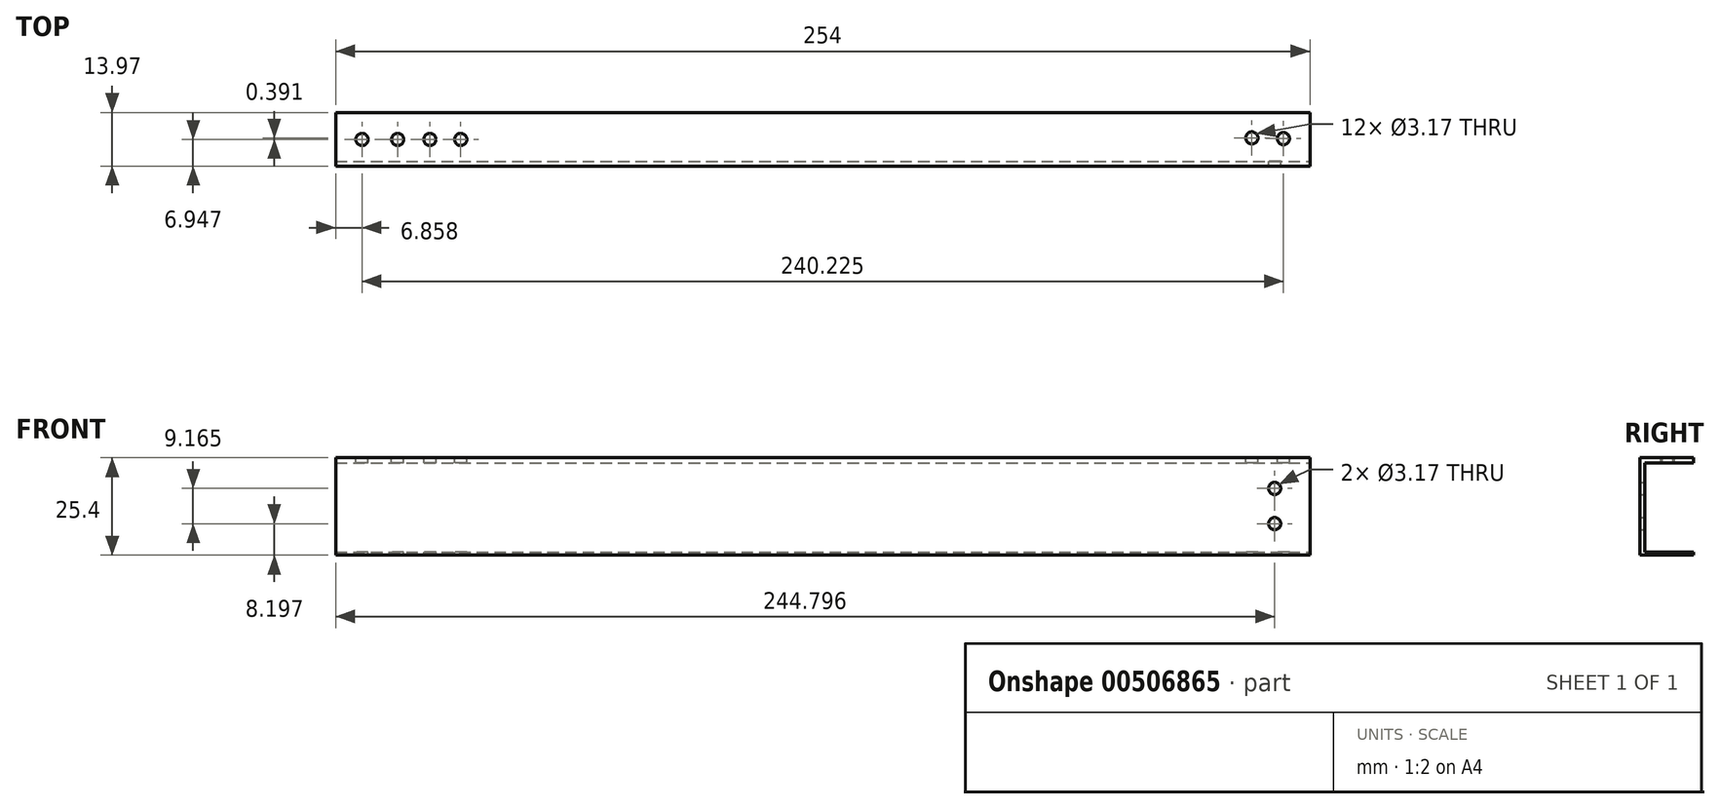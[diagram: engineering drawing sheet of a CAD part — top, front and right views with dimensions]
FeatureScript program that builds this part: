
annotation { "Feature Type Name" : "Feature", "Feature Type Description" : "" }
export const myFeature = defineFeature(function(context is Context, id is Id, definition is map)
    precondition{}
    {
        {
            var Q0;
            Q0=qCreatedBy(makeId("Front.planeOp"),FACE);
            var sketch = newSketch(context, id + "F0", { "sketchPlane" : qUnion([Q0])});
            skLineSegment(sketch, "E0.bottom", {"start": v(-123.25, 1.4) * mm, "end": v(130.75, 1.4) * mm});
            skLineSegment(sketch, "E0.top", {"start": v(-123.25, -24) * mm, "end": v(130.75, -24) * mm});
            skLineSegment(sketch, "E0.left", {"start": v(-123.25, 1.4) * mm, "end": v(-123.25, -24) * mm});
            skLineSegment(sketch, "E0.right", {"start": v(130.75, 1.4) * mm, "end": v(130.75, -24) * mm});
            skSolve(sketch);
        }
        {
            var Q0;
            Q0=makeQuery(id+"F0.imprint","IMPRINT",FACE,{"disambiguationData":[TD([[makeQuery(id+"F0.imprint","IMPRINT",EDGE,{"derivedFrom":sQuery(id+"F0.wireOp",EDGE,"E0.bottom")}),-1.0]])]});
            extrude(context, id + "F1", {"entities" : qUnion([Q0]), "depth" : 13.97 * mm, "offsetDistance" : 25.4 * mm});
        }
        {
            var Q0;
            Q0=qCreatedBy(makeId("Front.planeOp"),FACE);
            var sketch = newSketch(context, id + "F2", { "sketchPlane" : qUnion([Q0])});
            skLineSegment(sketch, "E1.bottom", {"start": v(-132.14, -23.19) * mm, "end": v(135.36, -23.19) * mm});
            skLineSegment(sketch, "E1.top", {"start": v(-132.14, 0) * mm, "end": v(135.36, 0) * mm});
            skLineSegment(sketch, "E1.left", {"start": v(-132.14, -23.19) * mm, "end": v(-132.14, 0) * mm});
            skLineSegment(sketch, "E1.right", {"start": v(135.36, -23.19) * mm, "end": v(135.36, 0) * mm});
            skSolve(sketch);
        }
        {
            var Q0;
            Q0=makeQuery(id+"F2.imprint","IMPRINT",FACE,{"disambiguationData":[TD([[makeQuery(id+"F2.imprint","IMPRINT",EDGE,{"derivedFrom":sQuery(id+"F2.wireOp",EDGE,"E1.bottom")}),1.0]])]});
            extrude(context, id + "F3", {"entities" : qUnion([Q0]), "operationType" : NewBodyOperationType.REMOVE, "depth" : 12.7 * mm, "offsetDistance" : 25.4 * mm});
        }
        {
            var Q0;
            Q0=makeQuery(id+"F1.opExtrude","SWEPT_FACE",FACE,{"disambiguationData":[OSD([sQuery(id+"F0.wireOp",EDGE,"E0.bottom")])]});
            var sketch = newSketch(context, id + "F4", { "sketchPlane" : qUnion([Q0])});
            skCircle(sketch, "E2", {"center": v(-116.4, -7.02) * mm, "radius": 2.87 * mm});
            skCircle(sketch, "E3", {"center": v(-107.1, -7.02) * mm, "radius": 2.68 * mm});
            skCircle(sketch, "E4", {"center": v(-98.69, -7.02) * mm, "radius": 2.66 * mm});
            skCircle(sketch, "E5", {"center": v(-90.64, -7.02) * mm, "radius": 2.91 * mm});
            skCircle(sketch, "E6", {"center": v(123.83, -6.82) * mm, "radius": 2.72 * mm});
            skCircle(sketch, "E7", {"center": v(115.61, -6.63) * mm, "radius": 3.06 * mm});
            skSolve(sketch);
        }
        {
            var Q0;
            Q0=sQuery(id+"F4.wireOp",VERTEX,"E6.center");
            var Q1;
            Q1=sQuery(id+"F4.wireOp",VERTEX,"E7.center");
            var Q2;
            Q2=sQuery(id+"F4.wireOp",VERTEX,"E2.center");
            var Q3;
            Q3=sQuery(id+"F4.wireOp",VERTEX,"E3.center");
            var Q4;
            Q4=sQuery(id+"F4.wireOp",VERTEX,"E4.center");
            var Q5;
            Q5=sQuery(id+"F4.wireOp",VERTEX,"E5.center");
            var Q6;
            Q6=makeQuery(id+"F1.opExtrude","SWEPT_BODY",BODY,{"disambiguationData":[OSD([sQuery(id+"F0.wireOp",EDGE,"E0.bottom"),sQuery(id+"F0.wireOp",EDGE,"E0.top"),sQuery(id+"F0.wireOp",EDGE,"E0.left"),sQuery(id+"F0.wireOp",EDGE,"E0.right")])]});
            hole(context, id + "F5", {"style" : HoleStyle.SIMPLE, "endStyle" : HoleEndStyle.THROUGH, "holeDiameter" : 3.17 * mm, "isTappedThrough" : true, "tappedDepth" : 12.7 * mm, "tapClearance" : 3, "locations" : qUnion([Q0, Q1, Q2, Q3, Q4, Q5]), "scope" : qUnion([Q6])});
        }
        {
            var Q0;
            Q0=qCreatedBy(makeId("Front.planeOp"),FACE);
            var sketch = newSketch(context, id + "F6", { "sketchPlane" : qUnion([Q0])});
            skCircle(sketch, "E8", {"center": v(121.55, -6.64) * mm, "radius": 2.16 * mm});
            skCircle(sketch, "E9", {"center": v(121.55, -15.8) * mm, "radius": 2.6 * mm});
            skSolve(sketch);
        }
        {
            var Q0;
            Q0=sQuery(id+"F6.wireOp",VERTEX,"E8.center");
            var Q1;
            Q1=sQuery(id+"F6.wireOp",VERTEX,"E9.center");
            var Q2;
            Q2=makeQuery(id+"F1.opExtrude","SWEPT_BODY",BODY,{"disambiguationData":[OSD([sQuery(id+"F0.wireOp",EDGE,"E0.bottom"),sQuery(id+"F0.wireOp",EDGE,"E0.top"),sQuery(id+"F0.wireOp",EDGE,"E0.left"),sQuery(id+"F0.wireOp",EDGE,"E0.right")])]});
            hole(context, id + "F7", {"style" : HoleStyle.SIMPLE, "endStyle" : HoleEndStyle.THROUGH, "oppositeDirection" : true, "holeDiameter" : 3.17 * mm, "isTappedThrough" : true, "tappedDepth" : 12.7 * mm, "tapClearance" : 3, "locations" : qUnion([Q0, Q1]), "scope" : qUnion([Q2])});
        }
    });
